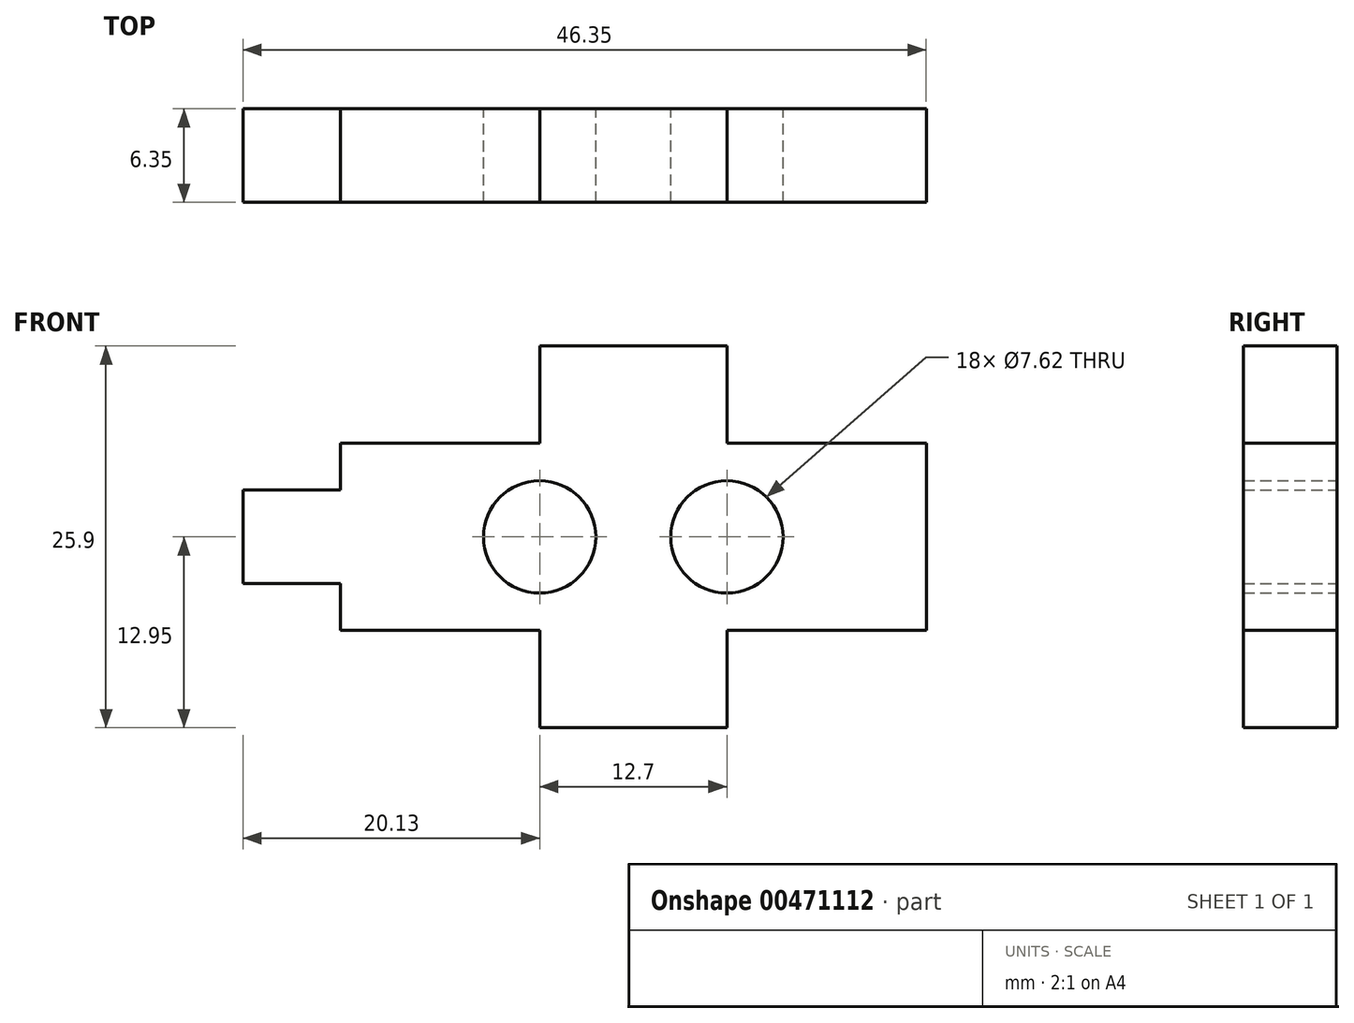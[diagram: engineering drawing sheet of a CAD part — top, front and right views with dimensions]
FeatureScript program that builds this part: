
annotation { "Feature Type Name" : "Feature", "Feature Type Description" : "" }
export const myFeature = defineFeature(function(context is Context, id is Id, definition is map)
    precondition{}
    {
        {
            var Q0;
            Q0=qCreatedBy(makeId("Front.planeOp"),FACE);
            var sketch = newSketch(context, id + "F0", { "sketchPlane" : qUnion([Q0])});
            skLineSegment(sketch, "E0", {"start": v(-6.35, 0) * mm, "end": v(-6.35, -6.6) * mm});
            skLineSegment(sketch, "E1", {"start": v(-6.35, 0) * mm, "end": v(-19.87, 0) * mm});
            skLineSegment(sketch, "E2", {"start": v(-19.87, 0) * mm, "end": v(-19.87, 3.17) * mm});
            skLineSegment(sketch, "E3", {"start": v(-19.87, 3.17) * mm, "end": v(-26.48, 3.17) * mm});
            skLineSegment(sketch, "E4", {"start": v(-26.48, 3.17) * mm, "end": v(-26.48, 9.52) * mm});
            skLineSegment(sketch, "E5.MirrorCS", {"start": v(-19.87, 9.52) * mm, "end": v(-26.48, 9.52) * mm});
            skLineSegment(sketch, "E6.MirrorCS", {"start": v(-6.35, 12.7) * mm, "end": v(-19.87, 12.7) * mm});
            skLineSegment(sketch, "E7.MirrorCS", {"start": v(-19.87, 12.7) * mm, "end": v(-19.87, 9.52) * mm});
            skLineSegment(sketch, "E8.MirrorCS", {"start": v(-6.35, 12.7) * mm, "end": v(-6.35, 19.3) * mm});
            skLineSegment(sketch, "E9.MirrorCS", {"start": v(6.35, 12.7) * mm, "end": v(19.87, 12.7) * mm});
            skLineSegment(sketch, "E10.MirrorCS", {"start": v(6.35, 12.7) * mm, "end": v(6.35, 19.3) * mm});
            skLineSegment(sketch, "E11.MirrorCS", {"start": v(6.35, 0) * mm, "end": v(19.87, 0) * mm});
            skLineSegment(sketch, "E12.MirrorCS", {"start": v(6.35, 0) * mm, "end": v(6.35, -6.6) * mm});
            skLineSegment(sketch, "E13", {"start": v(-6.35, 19.3) * mm, "end": v(6.35, 19.3) * mm});
            skLineSegment(sketch, "E14", {"start": v(6.35, -6.6) * mm, "end": v(-6.35, -6.6) * mm});
            skCircle(sketch, "E15", {"center": v(-6.35, 6.35) * mm, "radius": 3.81 * mm});
            skPoint(sketch, "E15.centerSnap0", {"position": v(-26.48, 6.35) * mm});
            skCircle(sketch, "E16.MirrorC", {"center": v(6.35, 6.35) * mm, "radius": 3.81 * mm});
            skLineSegment(sketch, "E17", {"start": v(19.87, 12.7) * mm, "end": v(19.87, 0) * mm});
            skSolve(sketch);
        }
        {
            var Q0;
            Q0=makeQuery(id+"F0.imprint","IMPRINT",FACE,{"disambiguationData":[TD([[makeQuery(id+"F0.imprint","IMPRINT",EDGE,{"derivedFrom":sQuery(id+"F0.wireOp",EDGE,"E0")}),1.0]])]});
            extrude(context, id + "F1", {"entities" : qUnion([Q0]), "depth" : 6.35 * mm});
        }
    });
